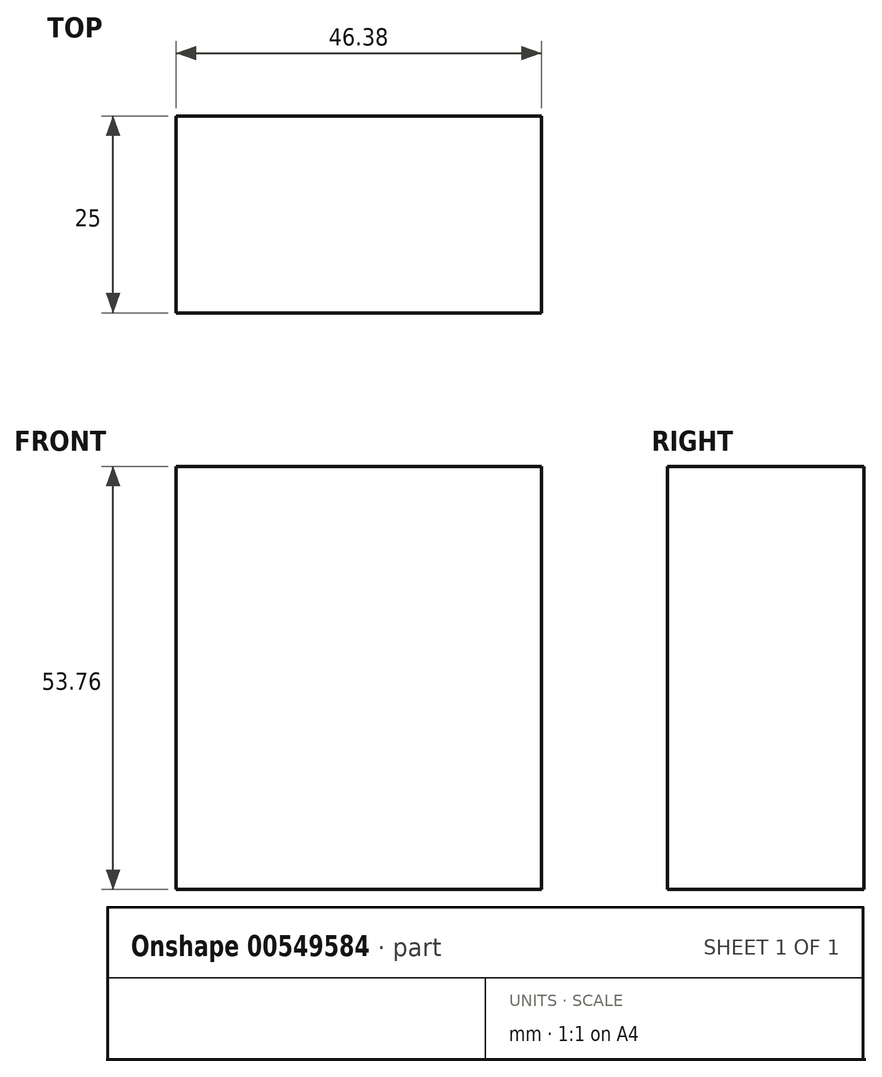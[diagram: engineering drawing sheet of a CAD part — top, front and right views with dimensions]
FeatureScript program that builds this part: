
annotation { "Feature Type Name" : "Feature", "Feature Type Description" : "" }
export const myFeature = defineFeature(function(context is Context, id is Id, definition is map)
    precondition{}
    {
        {
            var Q0;
            Q0=qCreatedBy(makeId("Front.planeOp"),FACE);
            var sketch = newSketch(context, id + "F0", { "sketchPlane" : qUnion([Q0])});
            skLineSegment(sketch, "E0.bottom", {"start": v(-120.44, 49.06) * mm, "end": v(-74.06, 49.06) * mm});
            skLineSegment(sketch, "E0.top", {"start": v(-120.44, -4.7) * mm, "end": v(-74.06, -4.7) * mm});
            skLineSegment(sketch, "E0.left", {"start": v(-120.44, 49.06) * mm, "end": v(-120.44, -4.7) * mm});
            skLineSegment(sketch, "E0.right", {"start": v(-74.06, 49.06) * mm, "end": v(-74.06, -4.7) * mm});
            skSolve(sketch);
        }
        {
            var Q0;
            Q0=makeQuery(id+"F0.imprint","IMPRINT",FACE,{"disambiguationData":[TD([[makeQuery(id+"F0.imprint","IMPRINT",EDGE,{"derivedFrom":sQuery(id+"F0.wireOp",EDGE,"E0.bottom")}),-1.0]])]});
            extrude(context, id + "F1", {"entities" : qUnion([Q0]), "depth" : 25 * mm, "offsetDistance" : 25 * mm});
        }
    });
